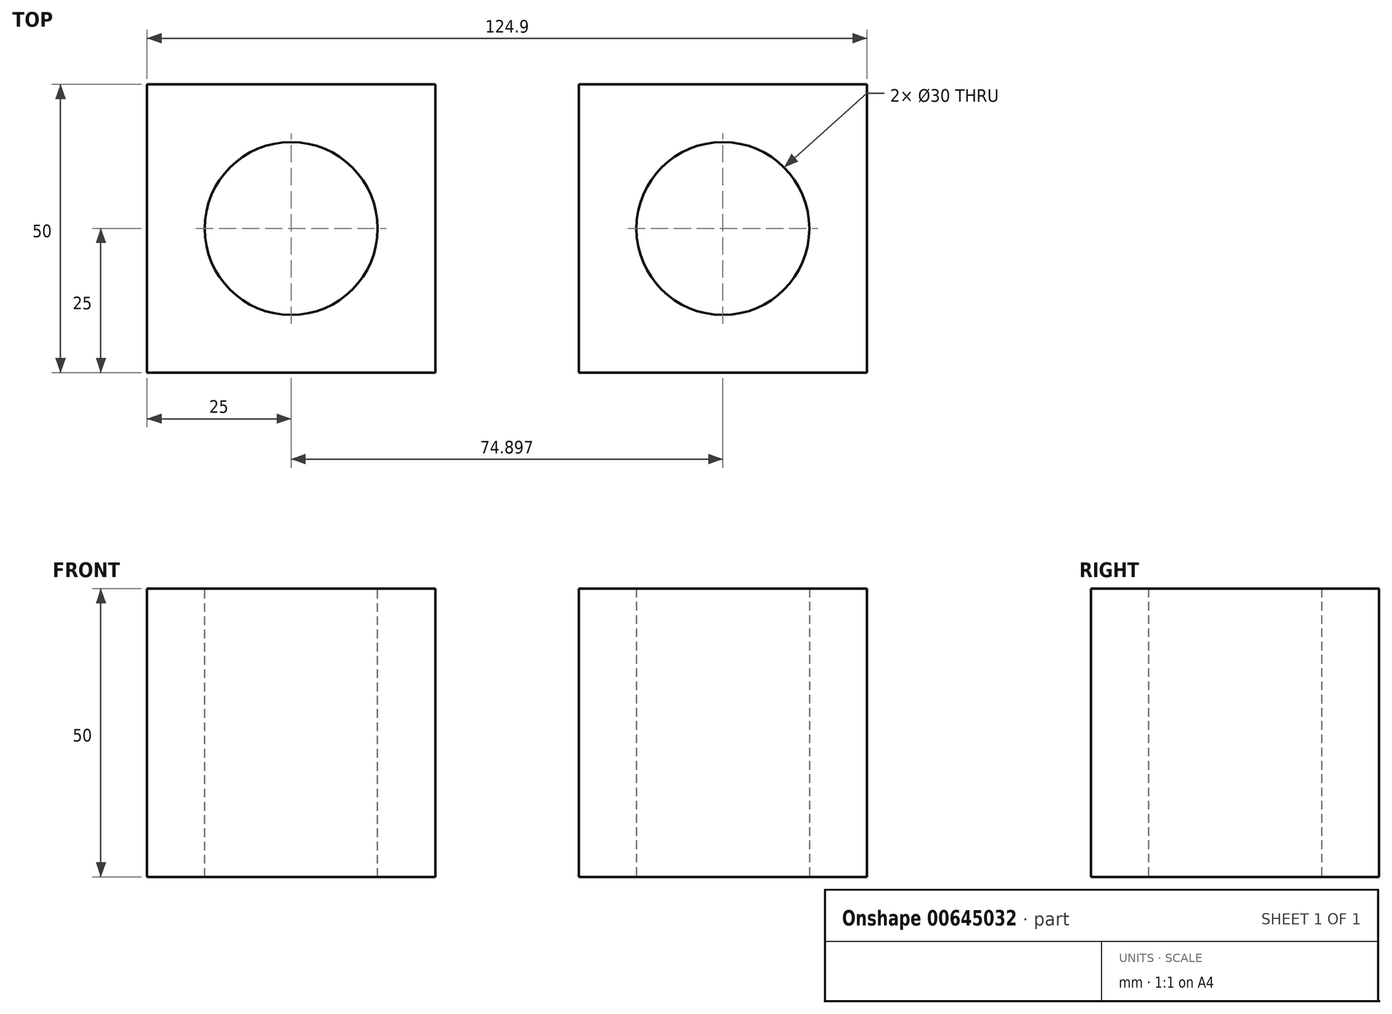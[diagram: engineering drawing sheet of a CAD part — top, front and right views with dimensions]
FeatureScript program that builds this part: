
annotation { "Feature Type Name" : "Feature", "Feature Type Description" : "" }
export const myFeature = defineFeature(function(context is Context, id is Id, definition is map)
    precondition{}
    {
        {
            var Q0;
            Q0=qCreatedBy(makeId("Top.planeOp"),FACE);
            var sketch = newSketch(context, id + "F0", { "sketchPlane" : qUnion([Q0])});
            skLineSegment(sketch, "E0.bottom", {"start": v(-25, 25) * mm, "end": v(25, 25) * mm});
            skLineSegment(sketch, "E0.top", {"start": v(-25, -25) * mm, "end": v(25, -25) * mm});
            skLineSegment(sketch, "E0.left", {"start": v(-25, 25) * mm, "end": v(-25, -25) * mm});
            skLineSegment(sketch, "E0.right", {"start": v(25, 25) * mm, "end": v(25, -25) * mm});
            skPoint(sketch, "E0.middle", {"position": v(0, 0) * mm});
            skSolve(sketch);
        }
        {
            var Q0;
            Q0 = qSketchRegion(id + "F0", true);
            extrude(context, id + "F1", {"entities" : qUnion([Q0]), "depth" : 50 * mm, "offsetDistance" : 25 * mm});
        }
        {
            var Q0;
            Q0=makeQuery(id+"F1.opExtrude","CAP_FACE",FACE,{"disambiguationData":[OSD([sQuery(id+"F0.wireOp",EDGE,"E0.bottom"),sQuery(id+"F0.wireOp",EDGE,"E0.top"),sQuery(id+"F0.wireOp",EDGE,"E0.left"),sQuery(id+"F0.wireOp",EDGE,"E0.right")])],"isStart":false});
            var sketch = newSketch(context, id + "F2", { "sketchPlane" : qUnion([Q0])});
            skCircle(sketch, "E1", {"center": v(0, 0) * mm, "radius": 15 * mm});
            skSolve(sketch);
        }
        {
            var Q0;
            Q0 = qSketchRegion(id + "F2", true);
            extrude(context, id + "F3", {"entities" : qUnion([Q0]), "operationType" : NewBodyOperationType.REMOVE, "oppositeDirection" : true, "depth" : 50 * mm, "offsetDistance" : 25 * mm});
        }
        {
            var Q0;
            Q0=qCreatedBy(makeId("Top.planeOp"),FACE);
            var sketch = newSketch(context, id + "F4", { "sketchPlane" : qUnion([Q0])});
            skLineSegment(sketch, "E2.bottom", {"start": v(49.9, 25) * mm, "end": v(99.9, 25) * mm});
            skLineSegment(sketch, "E2.top", {"start": v(49.9, -25) * mm, "end": v(99.9, -25) * mm});
            skLineSegment(sketch, "E2.left", {"start": v(49.9, 25) * mm, "end": v(49.9, -25) * mm});
            skLineSegment(sketch, "E2.right", {"start": v(99.9, 25) * mm, "end": v(99.9, -25) * mm});
            skPoint(sketch, "E2.middle", {"position": v(74.9, 0) * mm});
            skCircle(sketch, "E3", {"center": v(74.9, 0) * mm, "radius": 15 * mm});
            skSolve(sketch);
        }
        {
            var Q0;
            Q0 = qSketchRegion(id + "F4", true);
            extrude(context, id + "F5", {"entities" : qUnion([Q0]), "depth" : 50 * mm, "offsetDistance" : 25 * mm});
        }
        {
            var Q0;
            Q0 = qSketchRegion(id + "F4", true);
            extrude(context, id + "F6", {"entities" : qUnion([Q0]), "operationType" : NewBodyOperationType.ADD, "depth" : 50 * mm, "offsetDistance" : 25 * mm});
        }
    });
